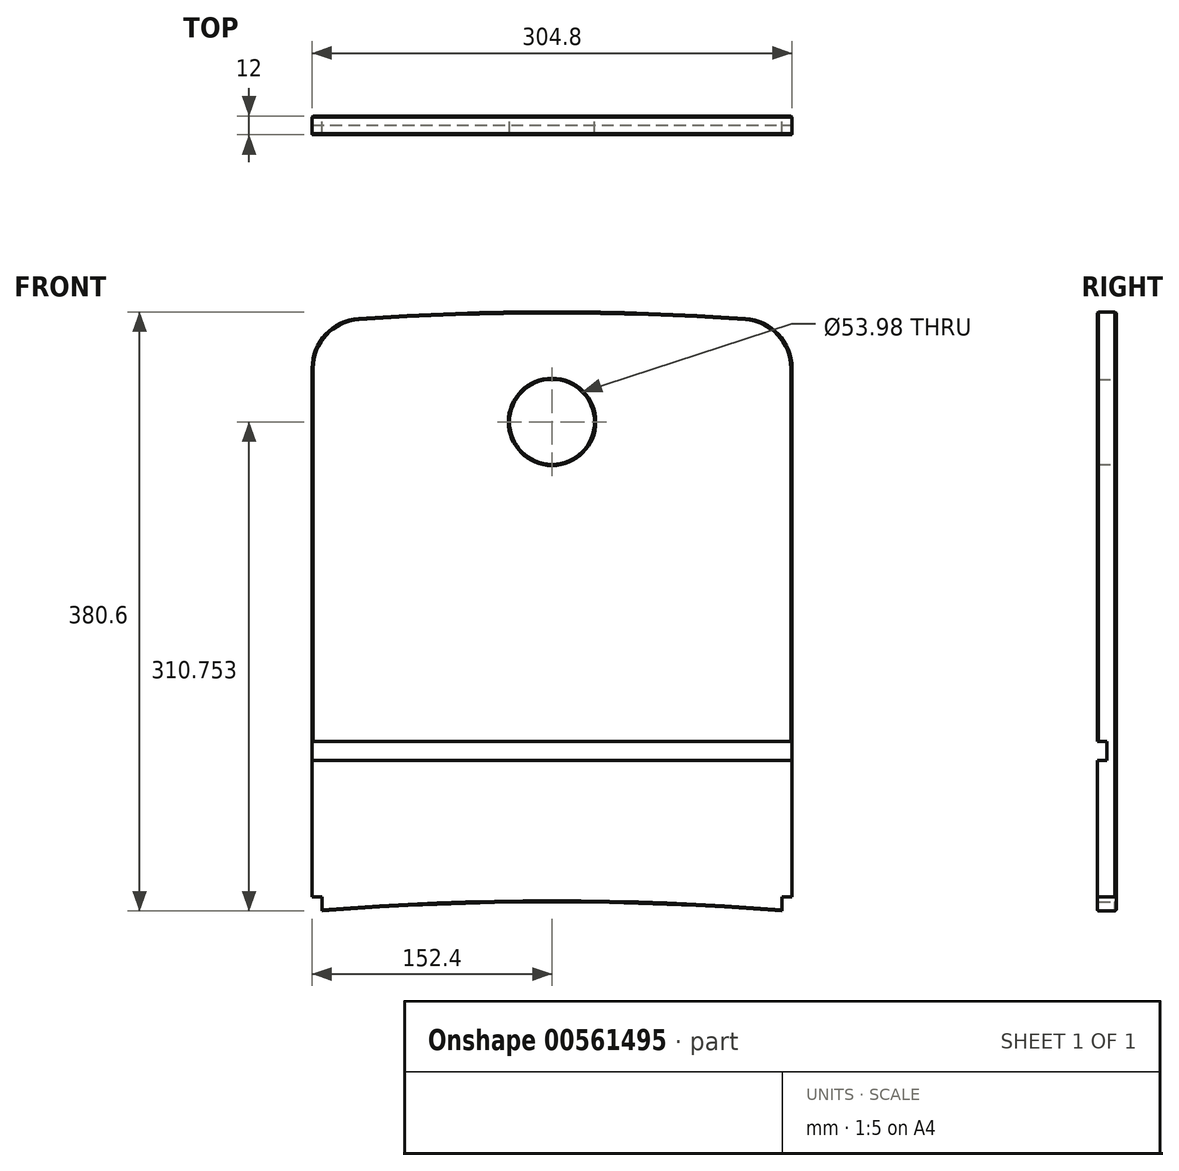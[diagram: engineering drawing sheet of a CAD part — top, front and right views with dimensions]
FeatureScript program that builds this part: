
annotation { "Feature Type Name" : "Feature", "Feature Type Description" : "" }
export const myFeature = defineFeature(function(context is Context, id is Id, definition is map)
    precondition{}
    {
        {
            var Q0;
            Q0=qCreatedBy(makeId("Front.planeOp"),FACE);
            var sketch = newSketch(context, id + "F0", { "sketchPlane" : qUnion([Q0])});
            skLineSegment(sketch, "E0", {"start": v(-146.05, 9) * mm, "end": v(-152.4, 9) * mm});
            skLineSegment(sketch, "E1", {"start": v(-152.4, 9) * mm, "end": v(-152.4, 344.8) * mm});
            skArc(sketch, "E2", {"start": v(-152.4, 344.8) * mm, "mid": v(-143.84, 366.5) * mm, "end": v(-122.78, 376.48) * mm});
            skArc(sketch, "E3", {"start": v(-122.78, 376.48) * mm, "mid": v(-61.42, 379.57) * mm, "end": v(0, 380.6) * mm});
            skLineSegment(sketch, "E4", {"start": v(0, 380.6) * mm, "end": v(0, 337.74) * mm});
            skLineSegment(sketch, "E5", {"start": v(-146.05, 9) * mm, "end": v(-146.05, 0) * mm});
            skArc(sketch, "E6", {"start": v(0, 5.83) * mm, "mid": v(-73.08, 4.37) * mm, "end": v(-146.05, 0) * mm});
            skLineSegment(sketch, "E7", {"start": v(0, 442.1) * mm, "end": v(0, -98.61) * mm, "construction": true});
            skLineSegment(sketch, "E8", {"start": v(-152.4, 9) * mm, "end": v(-152.4, -13.57) * mm, "construction": true});
            skArc(sketch, "E9", {"start": v(-146.05, 0) * mm, "mid": v(-149.23, -0.26) * mm, "end": v(-152.4, -0.52) * mm, "construction": true});
            skArc(sketch, "E10", {"start": v(0, 337.74) * mm, "mid": v(-26.99, 310.75) * mm, "end": v(0, 283.77) * mm});
            skLineSegment(sketch, "E11.trimOffspring", {"start": v(0, 283.77) * mm, "end": v(0, 5.83) * mm});
            skCircle(sketch, "E12", {"center": v(-149.23, 5.83) * mm, "radius": 3.18 * mm, "construction": true});
            skSolve(sketch);
        }
        {
            var Q0;
            Q0 = qSketchRegion(id + "F0", true);
            extrude(context, id + "F1", {"entities" : qUnion([Q0]), "depth" : 12 * mm, "offsetDistance" : 25.4 * mm, "symmetric" : true});
        }
        {
            var Q0;
            Q0=qCreatedBy(makeId("Front.planeOp"),FACE);
            var sketch = newSketch(context, id + "F2", { "sketchPlane" : qUnion([Q0])});
            skLineSegment(sketch, "E13.bottom", {"start": v(-152.4, 107.6) * mm, "end": v(0, 107.6) * mm});
            skLineSegment(sketch, "E13.top", {"start": v(-152.4, 95.6) * mm, "end": v(0, 95.6) * mm});
            skLineSegment(sketch, "E13.left", {"start": v(-152.4, 107.6) * mm, "end": v(-152.4, 95.6) * mm});
            skLineSegment(sketch, "E13.right", {"start": v(0, 107.6) * mm, "end": v(0, 95.6) * mm});
            skLineSegment(sketch, "E14", {"start": v(-152.4, 101.6) * mm, "end": v(0, 101.6) * mm, "construction": true});
            skSolve(sketch);
        }
        {
            var Q0;
            Q0 = qSketchRegion(id + "F2", true);
            extrude(context, id + "F3", {"entities" : qUnion([Q0]), "operationType" : NewBodyOperationType.REMOVE, "endBound" : BoundingType.THROUGH_ALL, "depth" : 25.4 * mm, "offsetDistance" : 25.4 * mm});
        }
        {
            var Q0;
            Q0=makeQuery(id+"F1.opExtrude","SWEPT_BODY",BODY,{"disambiguationData":[OSD([sQuery(id+"F0.wireOp",EDGE,"E0"),sQuery(id+"F0.wireOp",EDGE,"E1"),sQuery(id+"F0.wireOp",EDGE,"E2"),sQuery(id+"F0.wireOp",EDGE,"E3"),sQuery(id+"F0.wireOp",EDGE,"E4"),sQuery(id+"F0.wireOp",EDGE,"E5"),sQuery(id+"F0.wireOp",EDGE,"E6"),sQuery(id+"F0.wireOp",EDGE,"E10"),sQuery(id+"F0.wireOp",EDGE,"E11.trimOffspring")])]});
            var Q1;
            Q1=qCreatedBy(makeId("Right.planeOp"),FACE);
            mirror(context, id + "F4", {"operationType" : NewBodyOperationType.ADD, "entities" : qUnion([Q0]), "mirrorPlane" : qUnion([Q1])});
        }
        {
            var Q0;
            {var subQ0=makeQuery(id+"F1.opExtrude","CAP_EDGE",EDGE,{"disambiguationData":[OSD([sQuery(id+"F0.wireOp",EDGE,"E3")])],"isStart":true});Q0=makeQuery(id+"F4.boolean.opBoolean","MERGE",EDGE,{"derivedFrom":[subQ0,makeQuery(id+"F4.opPattern","COPY",EDGE,{"derivedFrom":subQ0,"instanceName":"1"})]});}
            var Q1;
            {var subQ0=makeQuery(id+"F1.opExtrude","CAP_EDGE",EDGE,{"disambiguationData":[OSD([sQuery(id+"F0.wireOp",EDGE,"E3")])],"isStart":false});Q1=makeQuery(id+"F4.boolean.opBoolean","MERGE",EDGE,{"derivedFrom":[subQ0,makeQuery(id+"F4.opPattern","COPY",EDGE,{"derivedFrom":subQ0,"instanceName":"1"})]});}
            var Q2;
            {var subQ0=makeQuery(id+"F1.opExtrude","CAP_EDGE",EDGE,{"disambiguationData":[OSD([sQuery(id+"F0.wireOp",EDGE,"E10")])],"isStart":false});Q2=makeQuery(id+"F4.boolean.opBoolean","MERGE",EDGE,{"derivedFrom":[subQ0,makeQuery(id+"F4.opPattern","COPY",EDGE,{"derivedFrom":subQ0,"instanceName":"1"})]});}
            var Q3;
            {var subQ0=makeQuery(id+"F1.opExtrude","CAP_EDGE",EDGE,{"disambiguationData":[OSD([sQuery(id+"F0.wireOp",EDGE,"E10")])],"isStart":true});Q3=makeQuery(id+"F4.boolean.opBoolean","MERGE",EDGE,{"derivedFrom":[subQ0,makeQuery(id+"F4.opPattern","COPY",EDGE,{"derivedFrom":subQ0,"instanceName":"1"})]});}
            var Q4;
            {var subQ0=makeQuery(id+"F1.opExtrude","CAP_EDGE",EDGE,{"disambiguationData":[OSD([sQuery(id+"F0.wireOp",EDGE,"E6")])],"isStart":true});Q4=makeQuery(id+"F4.boolean.opBoolean","MERGE",EDGE,{"derivedFrom":[subQ0,makeQuery(id+"F4.opPattern","COPY",EDGE,{"derivedFrom":subQ0,"instanceName":"1"})]});}
            var Q5;
            {var subQ0=makeQuery(id+"F1.opExtrude","CAP_EDGE",EDGE,{"disambiguationData":[OSD([sQuery(id+"F0.wireOp",EDGE,"E6")])],"isStart":false});Q5=makeQuery(id+"F4.boolean.opBoolean","MERGE",EDGE,{"derivedFrom":[subQ0,makeQuery(id+"F4.opPattern","COPY",EDGE,{"derivedFrom":subQ0,"instanceName":"1"})]});}
            chamfer(context, id + "F5", {"entities" : qUnion([Q0, Q1, Q2, Q3, Q4, Q5]), "width" : 0.76 * mm, "tangentPropagation" : true});
        }
    });
